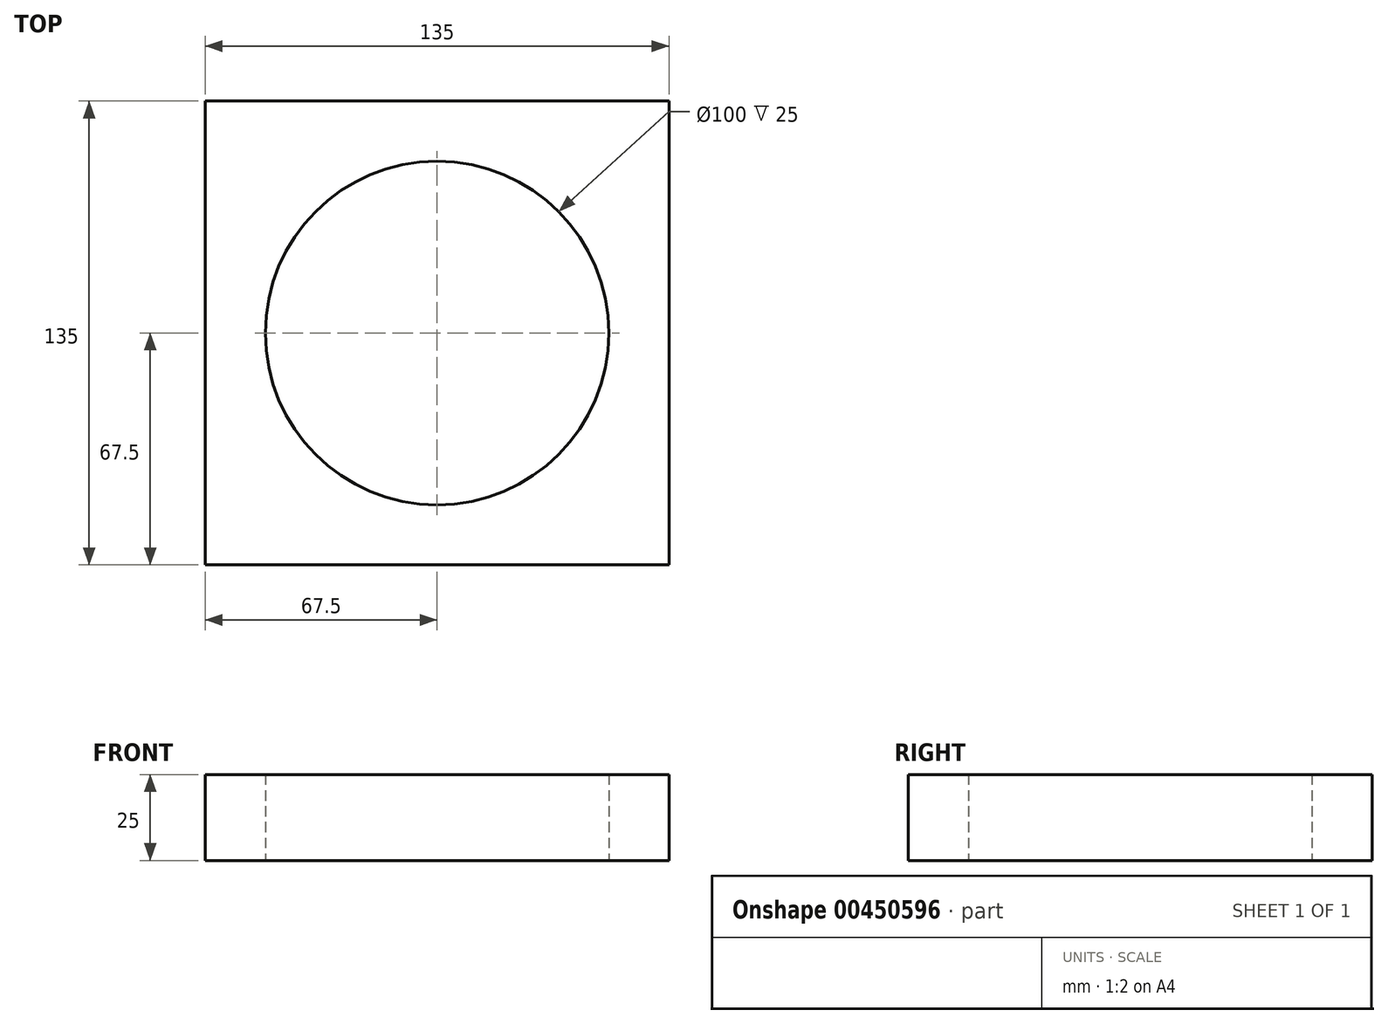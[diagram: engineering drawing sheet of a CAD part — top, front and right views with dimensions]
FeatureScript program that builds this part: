
annotation { "Feature Type Name" : "Feature", "Feature Type Description" : "" }
export const myFeature = defineFeature(function(context is Context, id is Id, definition is map)
    precondition{}
    {
        {
            var Q0;
            Q0=qCreatedBy(makeId("Top.planeOp"),FACE);
            var sketch = newSketch(context, id + "F0", { "sketchPlane" : qUnion([Q0])});
            skCircle(sketch, "E0", {"center": v(0, 0) * mm, "radius": 50 * mm});
            skLineSegment(sketch, "E1.bottom", {"start": v(-67.5, 67.5) * mm, "end": v(67.5, 67.5) * mm});
            skLineSegment(sketch, "E1.top", {"start": v(-67.5, -67.5) * mm, "end": v(67.5, -67.5) * mm});
            skLineSegment(sketch, "E1.left", {"start": v(-67.5, 67.5) * mm, "end": v(-67.5, -67.5) * mm});
            skLineSegment(sketch, "E1.right", {"start": v(67.5, 67.5) * mm, "end": v(67.5, -67.5) * mm});
            skLineSegment(sketch, "E2", {"start": v(0, 0) * mm, "end": v(46.6, -18.13) * mm});
            skSolve(sketch);
        }
        {
            var Q0;
            Q0 = qSketchRegion(id + "F0", true);
            extrude(context, id + "F1", {"entities" : qUnion([Q0]), "depth" : 25 * mm});
        }
    });
